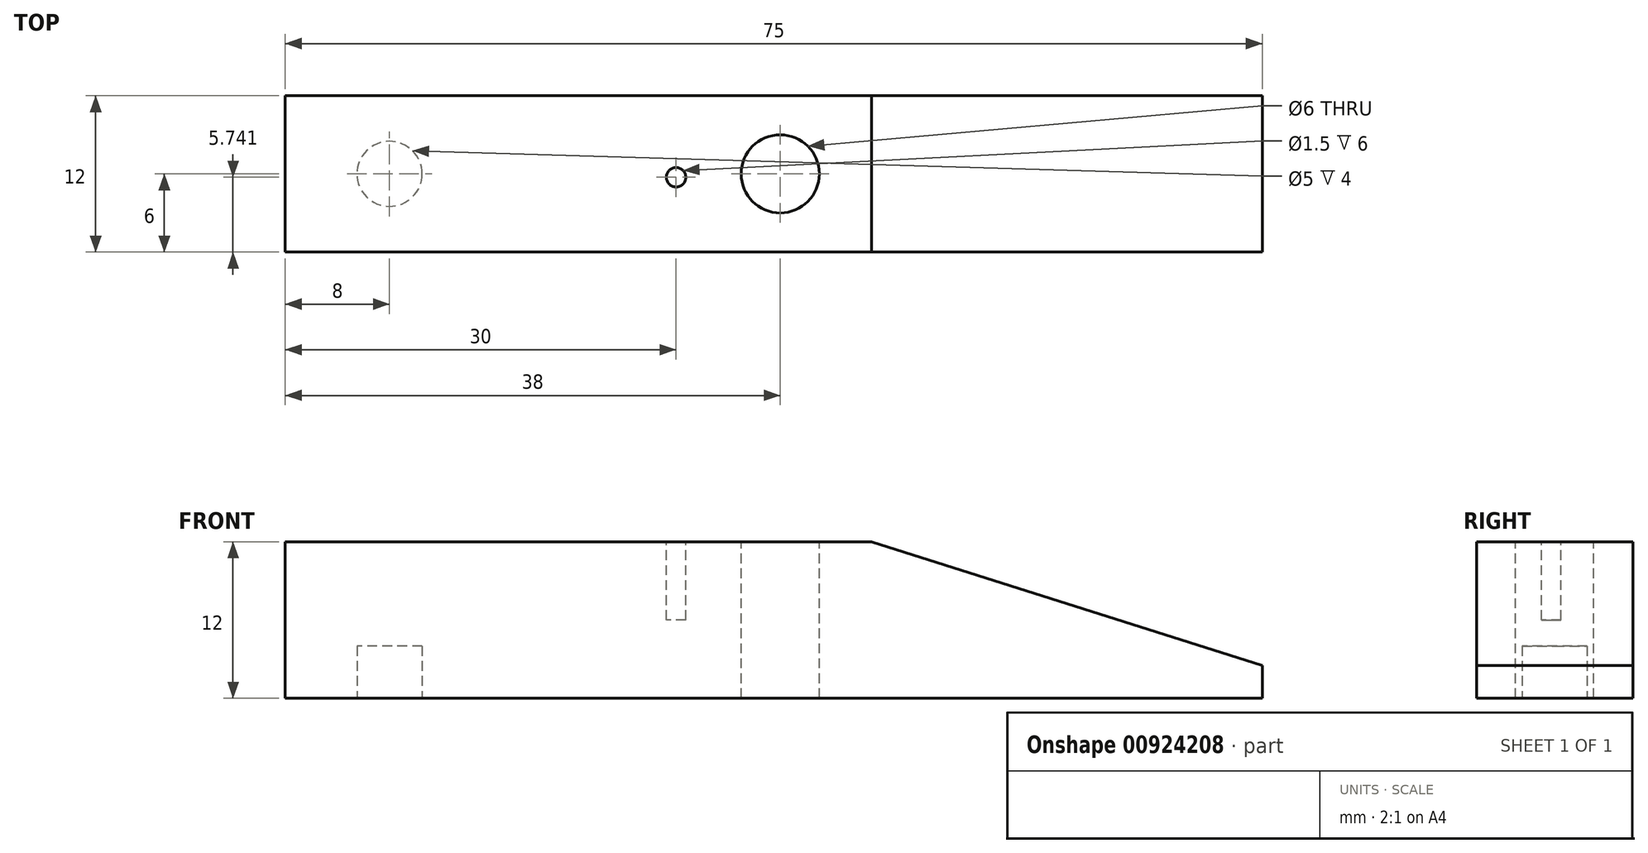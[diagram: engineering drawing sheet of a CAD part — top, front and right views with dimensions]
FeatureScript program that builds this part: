
annotation { "Feature Type Name" : "Feature", "Feature Type Description" : "" }
export const myFeature = defineFeature(function(context is Context, id is Id, definition is map)
    precondition{}
    {
        {
            var Q0;
            Q0=qCreatedBy(makeId("Front.planeOp"),FACE);
            var sketch = newSketch(context, id + "F0", { "sketchPlane" : qUnion([Q0])});
            skLineSegment(sketch, "E0", {"start": v(-45, 12) * mm, "end": v(-45, 0) * mm});
            skLineSegment(sketch, "E1", {"start": v(-45, 0) * mm, "end": v(30, 0) * mm});
            skLineSegment(sketch, "E2", {"start": v(30, 0) * mm, "end": v(30, 2.5) * mm});
            skLineSegment(sketch, "E3", {"start": v(30, 2.5) * mm, "end": v(0, 12) * mm});
            skLineSegment(sketch, "E4", {"start": v(0, 12) * mm, "end": v(-45, 12) * mm});
            skSolve(sketch);
        }
        {
            var Q0;
            Q0 = qSketchRegion(id + "F0", true);
            extrude(context, id + "F1", {"entities" : qUnion([Q0]), "depth" : 12 * mm, "offsetDistance" : 25 * mm});
        }
        {
            var Q0;
            Q0=makeQuery(id+"F1.opExtrude","SWEPT_FACE",FACE,{"disambiguationData":[OSD([sQuery(id+"F0.wireOp",EDGE,"E4")])]});
            var sketch = newSketch(context, id + "F2", { "sketchPlane" : qUnion([Q0])});
            skCircle(sketch, "E5", {"center": v(-7, -6) * mm, "radius": 3 * mm});
            skSolve(sketch);
        }
        {
            var Q0;
            Q0=makeQuery(id+"F2.imprint","IMPRINT",FACE,{"disambiguationData":[TD([[makeQuery(id+"F2.imprint","IMPRINT",EDGE,{"derivedFrom":sQuery(id+"F2.wireOp",EDGE,"E5")}),1.0]])]});
            extrude(context, id + "F3", {"entities" : qUnion([Q0]), "operationType" : NewBodyOperationType.REMOVE, "oppositeDirection" : true, "depth" : 25 * mm, "offsetDistance" : 25 * mm});
        }
        {
            var Q0;
            Q0=makeQuery(id+"F1.opExtrude","SWEPT_FACE",FACE,{"disambiguationData":[OSD([sQuery(id+"F0.wireOp",EDGE,"E4")])]});
            var sketch = newSketch(context, id + "F4", { "sketchPlane" : qUnion([Q0])});
            skCircle(sketch, "E6", {"center": v(-15, -6.26) * mm, "radius": 0.75 * mm});
            skSolve(sketch);
        }
        {
            var Q0;
            Q0 = qSketchRegion(id + "F4", true);
            extrude(context, id + "F5", {"entities" : qUnion([Q0]), "operationType" : NewBodyOperationType.REMOVE, "oppositeDirection" : true, "depth" : 6 * mm, "offsetDistance" : 25 * mm});
        }
        {
            var Q0;
            Q0=qCreatedBy(makeId("Top.planeOp"),FACE);
            var sketch = newSketch(context, id + "F6", { "sketchPlane" : qUnion([Q0])});
            skCircle(sketch, "E7", {"center": v(-37, -6) * mm, "radius": 2.5 * mm});
            skSolve(sketch);
        }
        {
            var Q0;
            Q0 = qSketchRegion(id + "F6", true);
            extrude(context, id + "F7", {"entities" : qUnion([Q0]), "operationType" : NewBodyOperationType.REMOVE, "depth" : 4 * mm, "offsetDistance" : 25 * mm});
        }
    });
